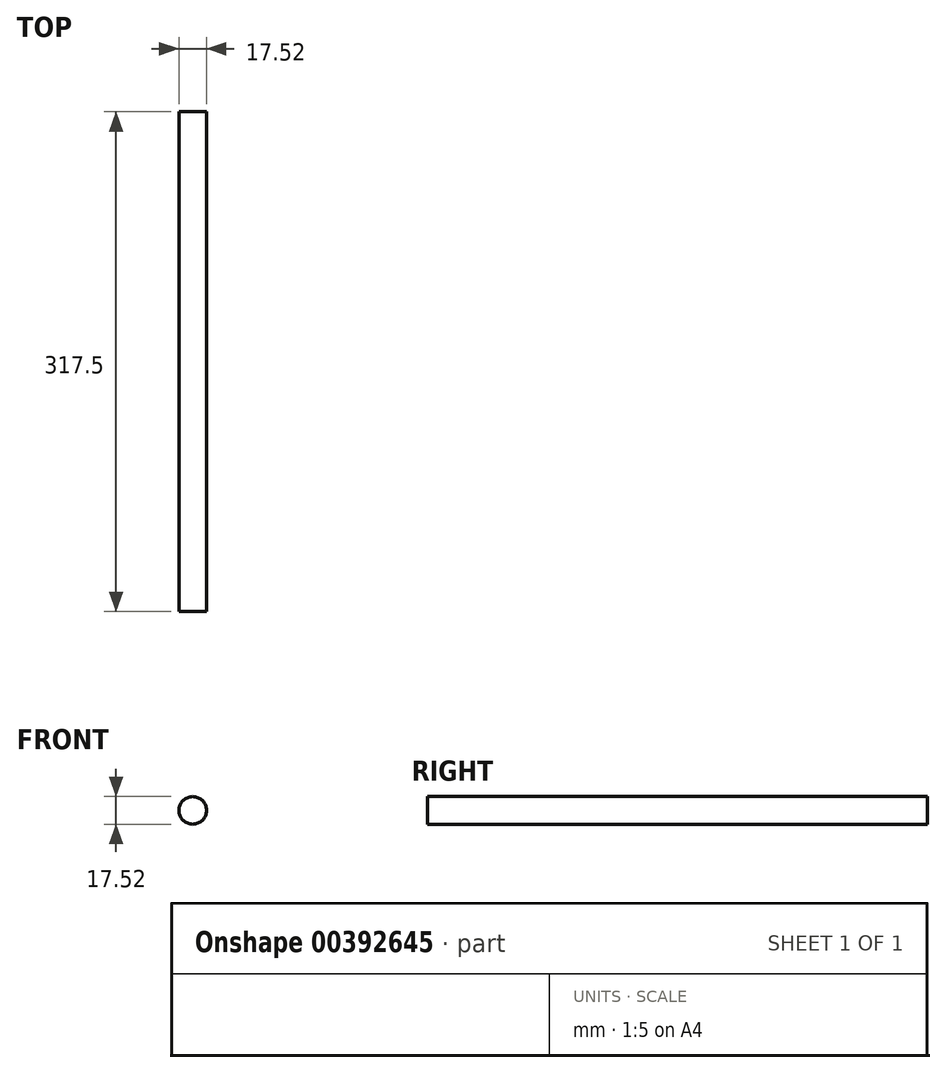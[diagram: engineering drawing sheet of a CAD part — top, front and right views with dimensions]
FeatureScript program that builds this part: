
annotation { "Feature Type Name" : "Feature", "Feature Type Description" : "" }
export const myFeature = defineFeature(function(context is Context, id is Id, definition is map)
    precondition{}
    {
        {
            var Q0;
            Q0=qCreatedBy(makeId("Front.planeOp"),FACE);
            var sketch = newSketch(context, id + "F0", { "sketchPlane" : qUnion([Q0])});
            skCircle(sketch, "E0", {"center": v(0, 0) * mm, "radius": 8.76 * mm});
            skSolve(sketch);
        }
        {
            var Q0;
            Q0=makeQuery(id+"F0.imprint","IMPRINT",FACE,{"disambiguationData":[TD([[makeQuery(id+"F0.imprint","IMPRINT",EDGE,{"derivedFrom":sQuery(id+"F0.wireOp",EDGE,"E0")}),1.0]])]});
            extrude(context, id + "F1", {"entities" : qUnion([Q0]), "depth" : 317.5 * mm});
        }
    });
